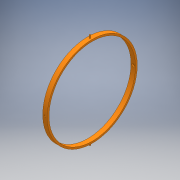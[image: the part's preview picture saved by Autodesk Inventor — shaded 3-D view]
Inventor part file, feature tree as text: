
AUTODESK INVENTOR PART (.ipt)
format: ipt  version: 2018 (Build 220112000, 112)  size: 158,720 bytes
history: native  units: mm
features: extrude x5, sketch x5, plane x3, mirror x2, projected_geometry x1
ambient origin geometry x8: Origin, YZ Plane, XZ Plane, XY Plane, X Axis, Y Axis, Z Axis, Center Point
bodies: Solid1 (feature_tree)
feature tree (16):
  extrude  "Extrusion1"  Depth=192.0mm
  plane  "Work Plane1"
  extrude  "Extrusion2"  Depth=10.0mm
  plane  "Work Plane2"
  extrude  "Extrusion3"  Depth=6.0mm
  mirror  "Mirror1"
  plane  "Work Plane3"
  extrude  "Extrusion4"  Depth=3.0mm
  mirror  "Mirror2"
  extrude  "Extrusion5"  Depth=12.0mm TaperAngle=0.0deg
  sketch  "Sketch1"  dims[d0=200.0mm d1=192.0mm]
  sketch  "Sketch2"  dims[d2=10.0mm d3=0.0mm d4=4.0mm]
  projected_geometry  "Projected Loop1"
  sketch  "Sketch3"  dims[d5=206.5mm d6=0.0mm d7=6.0mm]
  sketch  "Sketch4"  dims[d8=5.0mm d9=0.0mm d10=3.0mm]
  sketch  "Sketch5"  dims[d11=12.0mm d12=0.0mm d13=12.0mm d14=0.0mm]
